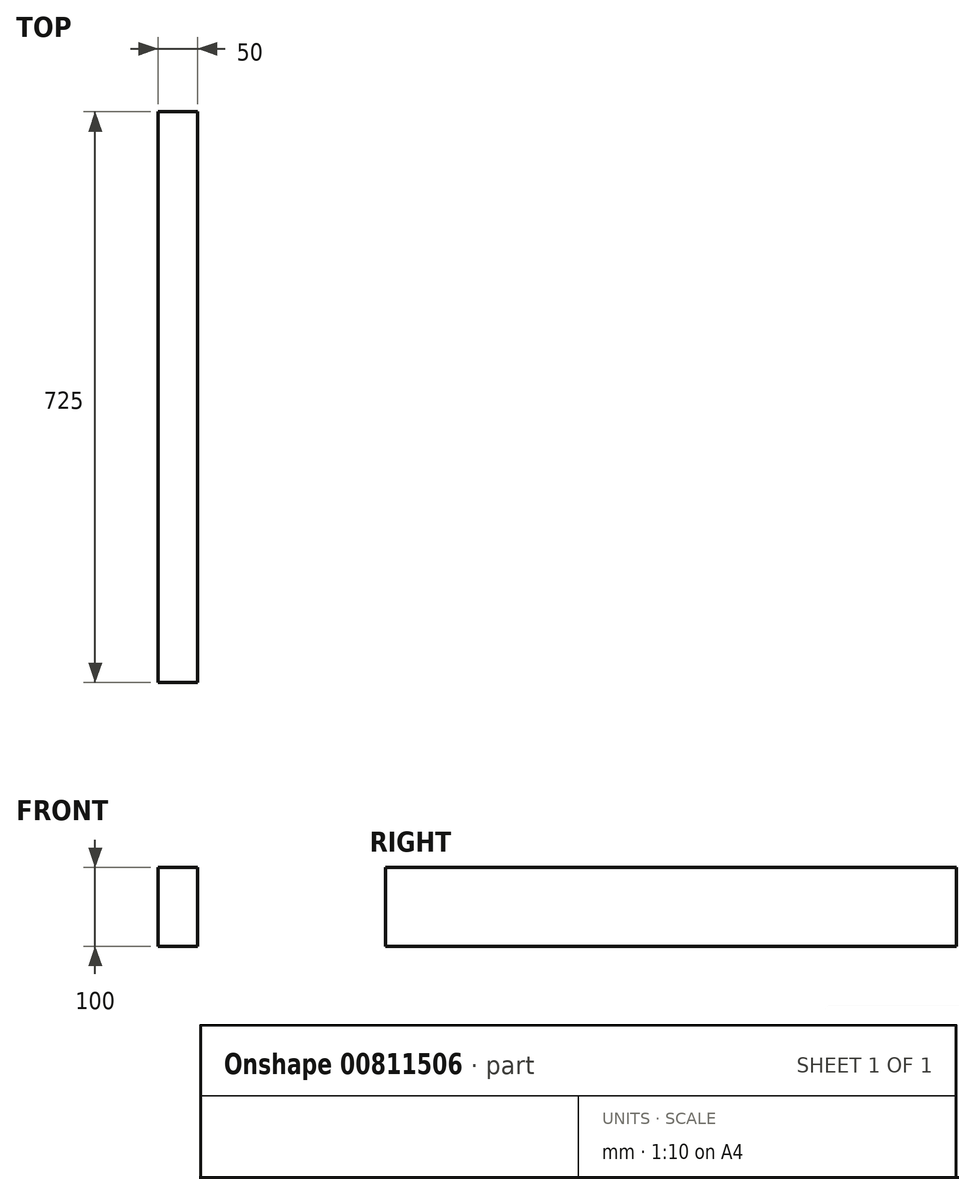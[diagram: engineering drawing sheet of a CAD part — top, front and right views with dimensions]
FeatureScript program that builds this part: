
annotation { "Feature Type Name" : "Feature", "Feature Type Description" : "" }
export const myFeature = defineFeature(function(context is Context, id is Id, definition is map)
    precondition{}
    {
        {
            var Q0;
            Q0=qCreatedBy(makeId("Front.planeOp"),FACE);
            var sketch = newSketch(context, id + "F0", { "sketchPlane" : qUnion([Q0])});
            skLineSegment(sketch, "E0.bottom", {"start": v(25, 50) * mm, "end": v(-25, 50) * mm});
            skLineSegment(sketch, "E0.top", {"start": v(25, -50) * mm, "end": v(-25, -50) * mm});
            skLineSegment(sketch, "E0.left", {"start": v(25, 50) * mm, "end": v(25, -50) * mm});
            skLineSegment(sketch, "E0.right", {"start": v(-25, 50) * mm, "end": v(-25, -50) * mm});
            skPoint(sketch, "E0.middle", {"position": v(0, 0) * mm});
            skSolve(sketch);
        }
        {
            var Q0;
            Q0=makeQuery(id+"F0.imprint","IMPRINT",FACE,{"disambiguationData":[TD([[makeQuery(id+"F0.imprint","IMPRINT",EDGE,{"derivedFrom":sQuery(id+"F0.wireOp",EDGE,"E0.bottom")}),1.0]])]});
            extrude(context, id + "F1", {"entities" : qUnion([Q0]), "endBound" : BoundingType.SYMMETRIC, "depth" : 725 * mm, "offsetDistance" : 25.4 * mm});
        }
    });
